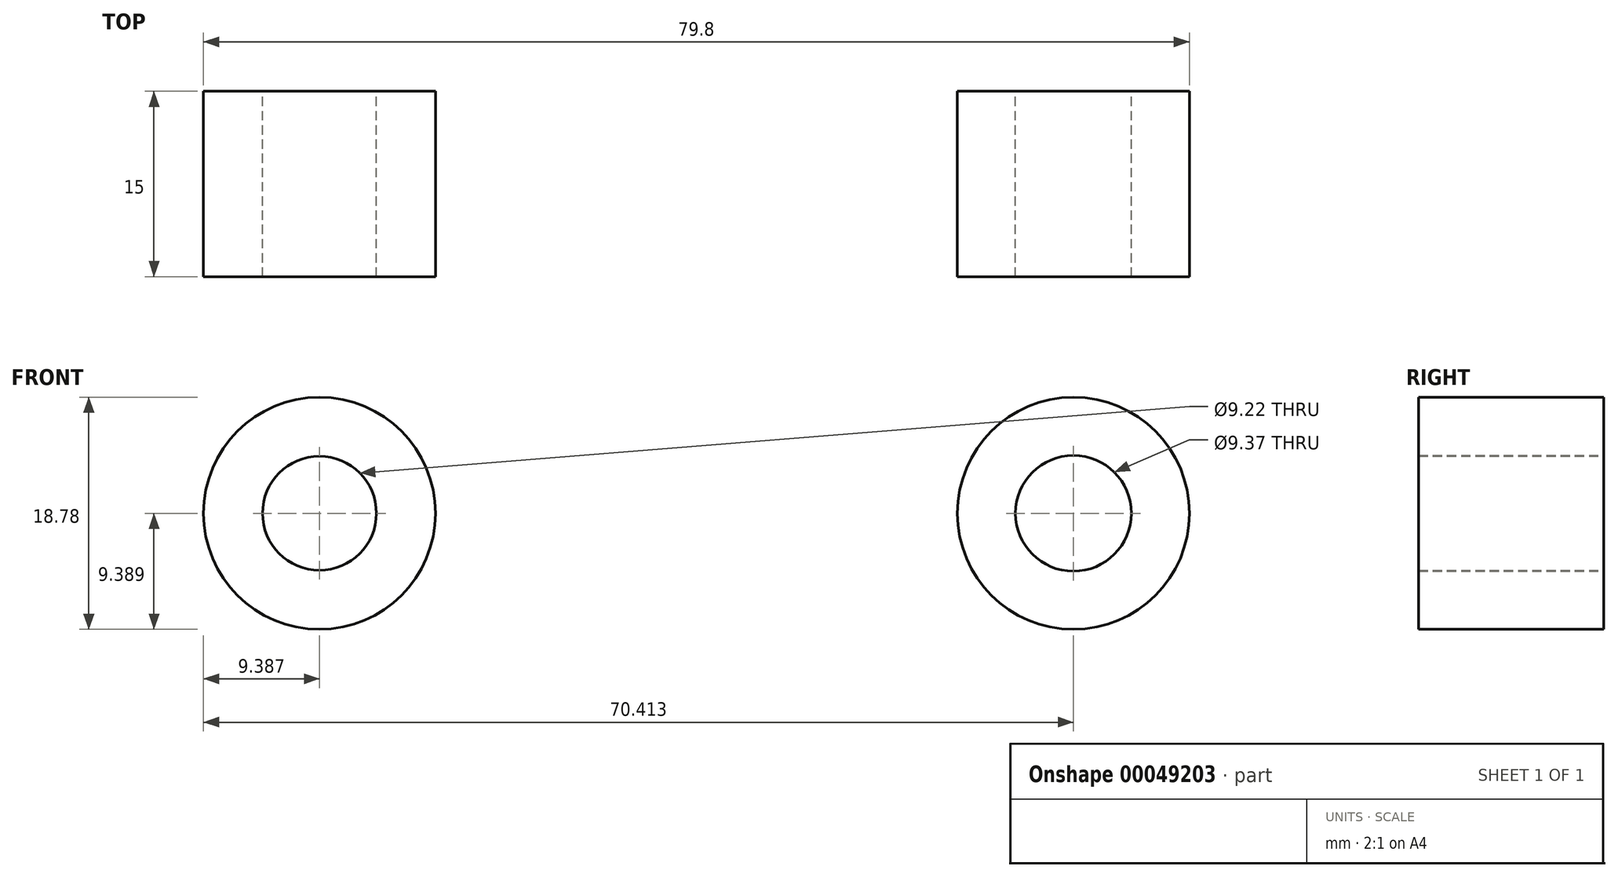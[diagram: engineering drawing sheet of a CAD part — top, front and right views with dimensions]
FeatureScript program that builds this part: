
annotation { "Feature Type Name" : "Feature", "Feature Type Description" : "" }
export const myFeature = defineFeature(function(context is Context, id is Id, definition is map)
    precondition{}
    {
        {
            var Q0;
            Q0=qCreatedBy(makeId("Front.planeOp"),FACE);
            var sketch = newSketch(context, id + "F0", { "sketchPlane" : qUnion([Q0])});
            skCircle(sketch, "E0", {"center": v(-42.63, -66.67) * mm, "radius": 9.39 * mm});
            skCircle(sketch, "E1", {"center": v(-42.63, -66.67) * mm, "radius": 4.61 * mm});
            skSolve(sketch);
        }
        {
            var Q0;
            Q0=qCreatedBy(makeId("Front.planeOp"),FACE);
            var sketch = newSketch(context, id + "F1", { "sketchPlane" : qUnion([Q0])});
            skCircle(sketch, "E2", {"center": v(18.4, -66.67) * mm, "radius": 9.39 * mm});
            skCircle(sketch, "E3", {"center": v(18.4, -66.67) * mm, "radius": 4.69 * mm});
            skSolve(sketch);
        }
        {
            var Q0;
            Q0=makeQuery(id+"F0.imprint","IMPRINT",FACE,{"disambiguationData":[TD([[makeQuery(id+"F0.imprint","IMPRINT",EDGE,{"derivedFrom":sQuery(id+"F0.wireOp",EDGE,"E0")}),1.0]])]});
            var Q1;
            Q1=makeQuery(id+"F1.imprint","IMPRINT",FACE,{"disambiguationData":[TD([[makeQuery(id+"F1.imprint","IMPRINT",EDGE,{"derivedFrom":sQuery(id+"F1.wireOp",EDGE,"E2")}),1.0]])]});
            extrude(context, id + "F2", {"entities" : qUnion([Q0, Q1]), "depth" : 15 * mm});
        }
    });
